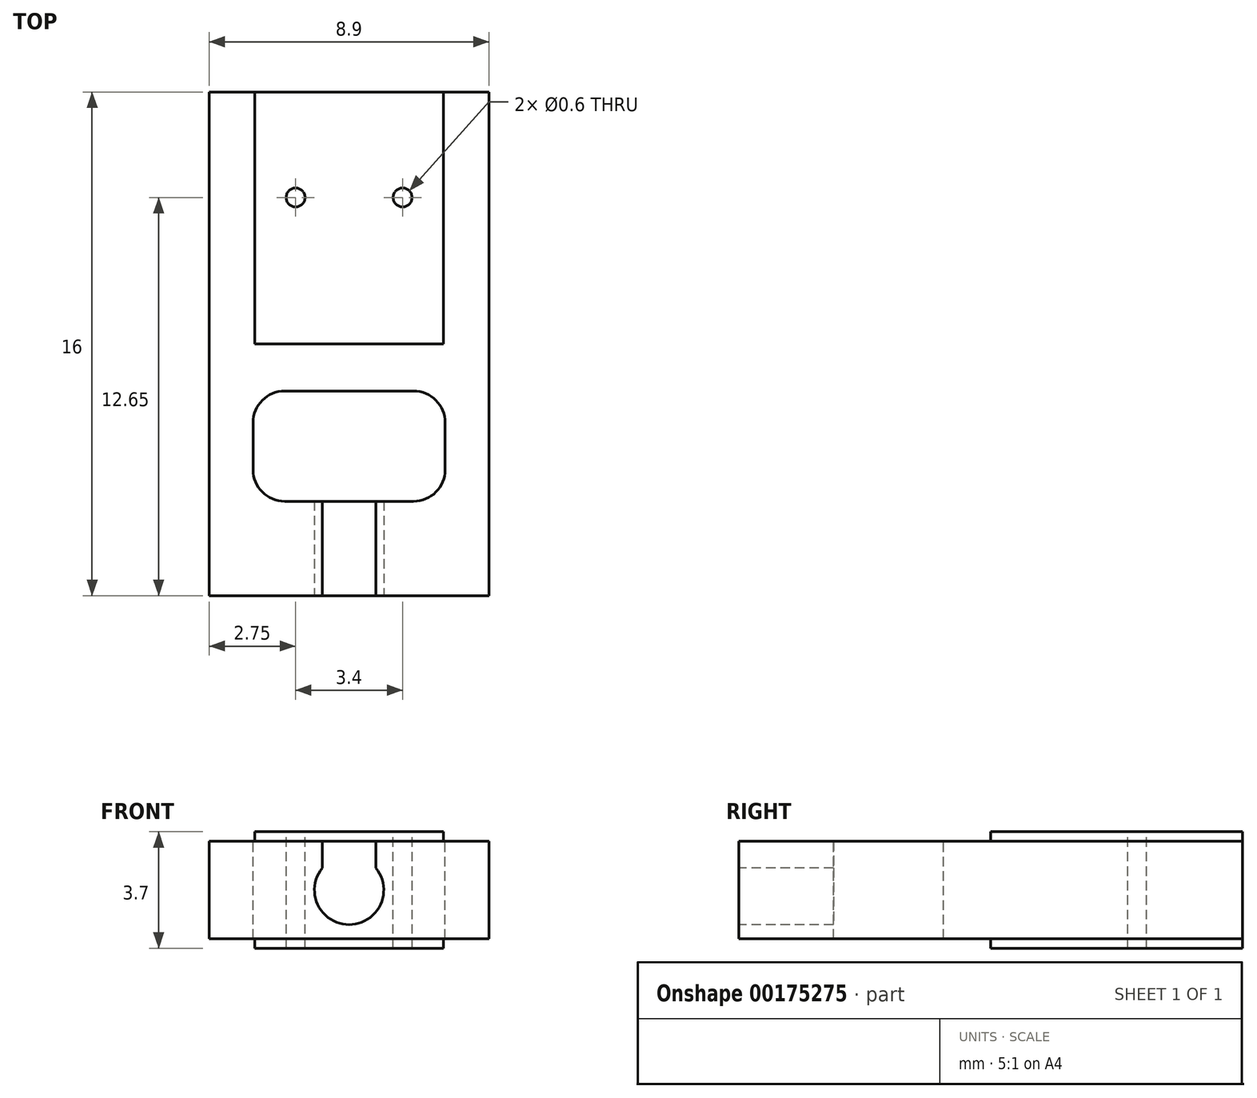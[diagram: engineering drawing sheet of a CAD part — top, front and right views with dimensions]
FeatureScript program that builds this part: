
annotation { "Feature Type Name" : "Feature", "Feature Type Description" : "" }
export const myFeature = defineFeature(function(context is Context, id is Id, definition is map)
    precondition{}
    {
        {
            assignVariable(context, id + "F0", {"name" : "Main_Width", "anyValue" : 8.9});
        }
        {
            assignVariable(context, id + "F1", {"name" : "Thickness1", "anyValue" : 3.1});
        }
        {
            assignVariable(context, id + "F2", {"name" : "Thickness2", "anyValue" : 3.7});
        }
        {
            var Q0;
            Q0=qCreatedBy(makeId("Right.planeOp"),FACE);
            var sketch = newSketch(context, id + "F3", { "sketchPlane" : qUnion([Q0])});
            skLineSegment(sketch, "E0", {"start": v(0, 0) * mm, "end": v(0, 1.55) * mm});
            skLineSegment(sketch, "E1", {"start": v(0, 1.55) * mm, "end": v(16, 1.55) * mm});
            skLineSegment(sketch, "E2", {"start": v(16, 1.55) * mm, "end": v(16, 0) * mm});
            skLineSegment(sketch, "E3", {"start": v(0, 0) * mm, "end": v(16, 0) * mm, "construction": true});
            skLineSegment(sketch, "E4.MirrorCS", {"start": v(0, -1.55) * mm, "end": v(16, -1.55) * mm});
            skLineSegment(sketch, "E5.MirrorCS", {"start": v(0, 0) * mm, "end": v(0, -1.55) * mm});
            skLineSegment(sketch, "E6.MirrorCS", {"start": v(16, -1.55) * mm, "end": v(16, 0) * mm});
            skSolve(sketch);
        }
        {
            var Q0;
            Q0=makeQuery(id+"F3.imprint","IMPRINT",FACE,{"disambiguationData":[TD([[makeQuery(id+"F3.imprint","IMPRINT",EDGE,{"derivedFrom":sQuery(id+"F3.wireOp",EDGE,"E0")}),-1.0]])]});
            extrude(context, id + "F4", {"entities" : qUnion([Q0]), "depth" : (getVariable(context, 'Main_Width')) * mm});
        }
        {
            var Q0;
            Q0=makeQuery(id+"F4.opExtrude","SWEPT_FACE",FACE,{"disambiguationData":[OSD([sQuery(id+"F3.wireOp",EDGE,"E1")])]});
            cPlane(context, id + "F5", {"entities" : qUnion([Q0]), "cplaneType" : CPlaneType.OFFSET, "offset" : ((getVariable(context, 'Thickness2') - getVariable(context, 'Thickness1')) / 2) * mm, "width" : 150 * mm, "height" : 150 * mm});
        }
        {
            var Q0;
            Q0=qCreatedBy(id+"F5.planeOp",FACE);
            var sketch = newSketch(context, id + "F6", { "sketchPlane" : qUnion([Q0])});
            skLineSegment(sketch, "E7.bottom", {"start": v(1.45, 16) * mm, "end": v(7.45, 16) * mm});
            skLineSegment(sketch, "E7.top", {"start": v(1.45, 8) * mm, "end": v(7.45, 8) * mm});
            skLineSegment(sketch, "E7.left", {"start": v(1.45, 16) * mm, "end": v(1.45, 8) * mm});
            skLineSegment(sketch, "E7.right", {"start": v(7.45, 16) * mm, "end": v(7.45, 8) * mm});
            skPoint(sketch, "E7.middle", {"position": v(4.45, 12) * mm});
            skLineSegment(sketch, "E8.0", {"start": v(8.9, 16) * mm, "end": v(0, 16) * mm});
            skLineSegment(sketch, "E9.0", {"start": v(0, 0) * mm, "end": v(0, 16) * mm});
            skPoint(sketch, "E10", {"position": v(4.45, 16) * mm});
            skPoint(sketch, "E11", {"position": v(0, 8) * mm});
            skSolve(sketch);
        }
        {
            var Q0;
            Q0=makeQuery(id+"F6.imprint","IMPRINT",FACE,{"disambiguationData":[TD([[makeQuery(id+"F6.imprint","IMPRINT",EDGE,{"derivedFrom":sQuery(id+"F6.wireOp",EDGE,"E7.top")}),1.0]])]});
            extrude(context, id + "F7", {"entities" : qUnion([Q0]), "operationType" : NewBodyOperationType.ADD, "oppositeDirection" : true, "depth" : (getVariable(context, 'Thickness2')) * mm});
        }
        {
            var Q0;
            Q0=qCreatedBy(id+"F5.planeOp",FACE);
            var sketch = newSketch(context, id + "F8", { "sketchPlane" : qUnion([Q0])});
            skLineSegment(sketch, "E12.0", {"start": v(8.9, 0) * mm, "end": v(0, 0) * mm});
            skLineSegment(sketch, "E13", {"start": v(4.45, 12.65) * mm, "end": v(4.45, 0) * mm, "construction": true});
            skPoint(sketch, "E13.endSnap0", {"position": v(4.45, 0) * mm});
            skLineSegment(sketch, "E14.bottom", {"start": v(2.4, 3) * mm, "end": v(6.5, 3) * mm});
            skLineSegment(sketch, "E14.top", {"start": v(2.4, 6.5) * mm, "end": v(6.5, 6.5) * mm});
            skLineSegment(sketch, "E14.left", {"start": v(2.4, 3) * mm, "end": v(2.4, 6.5) * mm, "construction": true});
            skLineSegment(sketch, "E14.right", {"start": v(6.5, 3) * mm, "end": v(6.5, 6.5) * mm, "construction": true});
            skPoint(sketch, "E14.middle", {"position": v(4.45, 4.75) * mm});
            skArc(sketch, "E15", {"start": v(1.4, 4) * mm, "mid": v(1.7, 3.3) * mm, "end": v(2.4, 3) * mm});
            skArc(sketch, "E16", {"start": v(2.4, 6.5) * mm, "mid": v(1.7, 6.2) * mm, "end": v(1.4, 5.5) * mm});
            skLineSegment(sketch, "E17", {"start": v(1.4, 4) * mm, "end": v(1.4, 5.5) * mm});
            skArc(sketch, "E18.MirrorCS", {"start": v(6.5, 6.5) * mm, "mid": v(7.2, 6.2) * mm, "end": v(7.5, 5.5) * mm});
            skLineSegment(sketch, "E19.MirrorCS", {"start": v(7.5, 4) * mm, "end": v(7.5, 5.5) * mm});
            skArc(sketch, "E20.MirrorCS", {"start": v(7.5, 4) * mm, "mid": v(7.2, 3.3) * mm, "end": v(6.5, 3) * mm});
            skCircle(sketch, "E21", {"center": v(2.75, 12.65) * mm, "radius": 0.3 * mm});
            skCircle(sketch, "E22", {"center": v(6.15, 12.65) * mm, "radius": 0.3 * mm});
            skSolve(sketch);
        }
        {
            var Q0;
            Q0=makeQuery(id+"F8.imprint","IMPRINT",FACE,{"disambiguationData":[TD([[makeQuery(id+"F8.imprint","IMPRINT",EDGE,{"derivedFrom":sQuery(id+"F8.wireOp",EDGE,"E14.bottom")}),1.0]])]});
            var Q1;
            Q1=makeQuery(id+"F8.imprint","IMPRINT",FACE,{"disambiguationData":[TD([[makeQuery(id+"F8.imprint","IMPRINT",EDGE,{"derivedFrom":sQuery(id+"F8.wireOp",EDGE,"E21")}),1.0]])]});
            var Q2;
            Q2=makeQuery(id+"F8.imprint","IMPRINT",FACE,{"disambiguationData":[TD([[makeQuery(id+"F8.imprint","IMPRINT",EDGE,{"derivedFrom":sQuery(id+"F8.wireOp",EDGE,"E22")}),1.0]])]});
            extrude(context, id + "F9", {"entities" : qUnion([Q0, Q1, Q2]), "operationType" : NewBodyOperationType.REMOVE, "endBound" : BoundingType.THROUGH_ALL, "oppositeDirection" : true, "depth" : 25 * mm});
        }
        {
            var Q0;
            Q0=makeQuery(id+"F4.opExtrude","SWEPT_FACE",FACE,{"disambiguationData":[OSD([sQuery(id+"F3.wireOp",EDGE,"E0"),sQuery(id+"F3.wireOp",EDGE,"E5.MirrorCS")])]});
            var sketch = newSketch(context, id + "F10", { "sketchPlane" : qUnion([Q0])});
            skLineSegment(sketch, "E23.0.0", {"start": v(0, 1.55) * mm, "end": v(0, -1.55) * mm});
            skLineSegment(sketch, "E23.0.1", {"start": v(0, -1.55) * mm, "end": v(8.9, -1.55) * mm});
            skLineSegment(sketch, "E23.0.2", {"start": v(8.9, -1.55) * mm, "end": v(8.9, 1.55) * mm});
            skLineSegment(sketch, "E23.0.3", {"start": v(8.9, 1.55) * mm, "end": v(0, 1.55) * mm});
            skArc(sketch, "E24", {"start": v(3.6, 0.7) * mm, "mid": v(4.45, -1.1) * mm, "end": v(5.3, 0.7) * mm});
            skLineSegment(sketch, "E25", {"start": v(4.45, 1.55) * mm, "end": v(4.45, -1.55) * mm, "construction": true});
            skLineSegment(sketch, "E26", {"start": v(3.6, 0.7) * mm, "end": v(3.6, 1.55) * mm});
            skLineSegment(sketch, "E27", {"start": v(5.3, 0.7) * mm, "end": v(5.3, 1.55) * mm});
            skSolve(sketch);
        }
        {
            var Q0;
            Q0=makeQuery(id+"F10.imprint","IMPRINT",FACE,{"disambiguationData":[TD([[makeQuery(id+"F10.imprint","IMPRINT",EDGE,{"derivedFrom":sQuery(id+"F10.wireOp",EDGE,"E24")}),1.0]])]});
            extrude(context, id + "F11", {"entities" : qUnion([Q0]), "operationType" : NewBodyOperationType.REMOVE, "endBound" : BoundingType.UP_TO_NEXT, "oppositeDirection" : true, "depth" : 25 * mm});
        }
    });
